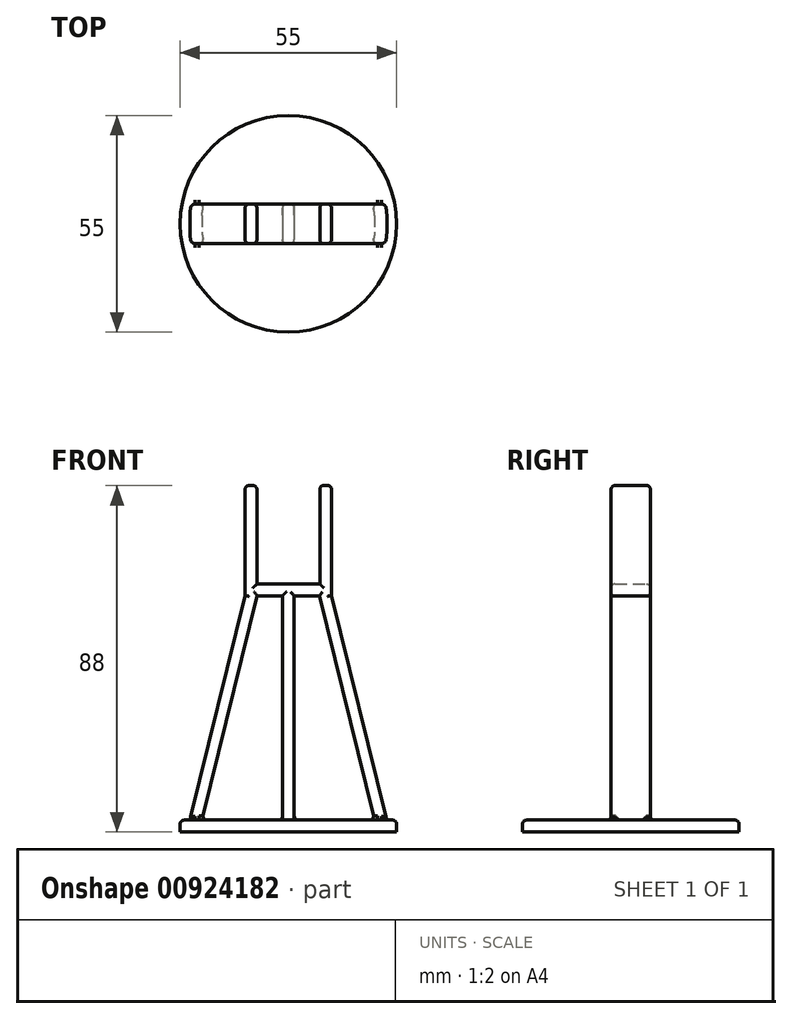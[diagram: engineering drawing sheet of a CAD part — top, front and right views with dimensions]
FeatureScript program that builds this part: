
annotation { "Feature Type Name" : "Feature", "Feature Type Description" : "" }
export const myFeature = defineFeature(function(context is Context, id is Id, definition is map)
    precondition{}
    {
        {
            var Q0;
            Q0=qCreatedBy(makeId("Front.planeOp"),FACE);
            var sketch = newSketch(context, id + "F0", { "sketchPlane" : qUnion([Q0])});
            skLineSegment(sketch, "E0.left", {"start": v(8, 12.5) * mm, "end": v(8, -12.5) * mm});
            skLineSegment(sketch, "E0.right", {"start": v(-8, 12.5) * mm, "end": v(-8, -12.5) * mm});
            skPoint(sketch, "E0.middle", {"position": v(0, 0) * mm});
            skLineSegment(sketch, "E1.top", {"start": v(-25, -72.5) * mm, "end": v(25, -72.5) * mm});
            skLineSegment(sketch, "E2", {"start": v(8, -12.5) * mm, "end": v(-8, -12.5) * mm});
            skLineSegment(sketch, "E3.0", {"start": v(11, 12.5) * mm, "end": v(11, -15.5) * mm});
            skLineSegment(sketch, "E3.1", {"start": v(11, -15.5) * mm, "end": v(-11, -15.5) * mm});
            skLineSegment(sketch, "E3.2", {"start": v(-11, 12.5) * mm, "end": v(-11, -15.5) * mm});
            skLineSegment(sketch, "E4", {"start": v(-8, 12.5) * mm, "end": v(-11, 12.5) * mm});
            skLineSegment(sketch, "E5", {"start": v(8, 12.5) * mm, "end": v(11, 12.5) * mm});
            skLineSegment(sketch, "E6", {"start": v(-11, -15.5) * mm, "end": v(-25, -72.5) * mm});
            skLineSegment(sketch, "E7", {"start": v(11, -15.5) * mm, "end": v(25, -72.5) * mm});
            skSolve(sketch);
        }
        {
            var Q0;
            Q0 = qSketchRegion(id + "F0", true);
            extrude(context, id + "F1", {"entities" : qUnion([Q0]), "depth" : 10 * mm, "offsetDistance" : 25 * mm});
        }
        {
            var Q0;
            Q0=makeQuery(id+"F1.opExtrude","CAP_FACE",FACE,{"disambiguationData":[OSD([sQuery(id+"F0.wireOp",EDGE,"E0.left"),sQuery(id+"F0.wireOp",EDGE,"E0.right"),sQuery(id+"F0.wireOp",EDGE,"E1.top"),sQuery(id+"F0.wireOp",EDGE,"E2"),sQuery(id+"F0.wireOp",EDGE,"E3.0"),sQuery(id+"F0.wireOp",EDGE,"E3.2"),sQuery(id+"F0.wireOp",EDGE,"E4"),sQuery(id+"F0.wireOp",EDGE,"E5"),sQuery(id+"F0.wireOp",EDGE,"E6"),sQuery(id+"F0.wireOp",EDGE,"E7")])],"isStart":false});
            var sketch = newSketch(context, id + "F2", { "sketchPlane" : qUnion([Q0])});
            skLineSegment(sketch, "E8", {"start": v(-11, -15.5) * mm, "end": v(11, -15.5) * mm, "construction": true});
            skLineSegment(sketch, "E9", {"start": v(-7.91, -15.5) * mm, "end": v(-21.91, -72.5) * mm});
            skLineSegment(sketch, "E10", {"start": v(-21.91, -72.5) * mm, "end": v(-1.5, -72.5) * mm});
            skLineSegment(sketch, "E11", {"start": v(-1.5, -72.5) * mm, "end": v(-1.5, -15.5) * mm});
            skLineSegment(sketch, "E12", {"start": v(-1.5, -15.5) * mm, "end": v(-7.91, -15.5) * mm});
            skLineSegment(sketch, "E13.MirrorCS", {"start": v(1.5, -72.5) * mm, "end": v(1.5, -15.5) * mm});
            skLineSegment(sketch, "E14.MirrorCS", {"start": v(7.91, -15.5) * mm, "end": v(21.91, -72.5) * mm});
            skLineSegment(sketch, "E15.MirrorCS", {"start": v(11, -15.5) * mm, "end": v(-11, -15.5) * mm, "construction": true});
            skLineSegment(sketch, "E16.MirrorCS", {"start": v(21.91, -72.5) * mm, "end": v(1.5, -72.5) * mm});
            skLineSegment(sketch, "E17", {"start": v(7.91, -15.5) * mm, "end": v(1.5, -15.5) * mm});
            skSolve(sketch);
        }
        {
            var Q0;
            Q0 = qSketchRegion(id + "F2", true);
            extrude(context, id + "F3", {"entities" : qUnion([Q0]), "operationType" : NewBodyOperationType.REMOVE, "oppositeDirection" : true, "depth" : 25 * mm, "offsetDistance" : 25 * mm});
        }
        {
            var Q0;
            Q0=makeQuery(id+"F1.opExtrude","SWEPT_FACE",FACE,{"disambiguationData":[OSD([sQuery(id+"F0.wireOp",EDGE,"E1.top")])]});
            var sketch = newSketch(context, id + "F4", { "sketchPlane" : qUnion([Q0])});
            skCircle(sketch, "E18", {"center": v(0, 5) * mm, "radius": 27.5 * mm});
            skLineSegment(sketch, "E19", {"start": v(0, 5) * mm, "end": v(0, 0) * mm, "construction": true});
            skLineSegment(sketch, "E20", {"start": v(0, 5) * mm, "end": v(0, 10) * mm, "construction": true});
            skLineSegment(sketch, "E21", {"start": v(0, 5) * mm, "end": v(-1.5, 5) * mm, "construction": true});
            skLineSegment(sketch, "E22", {"start": v(0, 5) * mm, "end": v(1.5, 5) * mm, "construction": true});
            skSolve(sketch);
        }
        {
            var Q0;
            Q0 = qSketchRegion(id + "F4", true);
            extrude(context, id + "F5", {"entities" : qUnion([Q0]), "operationType" : NewBodyOperationType.ADD, "depth" : 3 * mm, "offsetDistance" : 25 * mm});
        }
        {
            var Q0;
            Q0=makeQuery(id+"F1.opExtrude","SWEPT_EDGE",EDGE,{"disambiguationData":[OSD([sQuery(id+"F0.wireOp",EDGE,"E0.right"),sQuery(id+"F0.wireOp",EDGE,"E4")])]});
            var Q1;
            Q1=makeQuery(id+"F1.opExtrude","SWEPT_EDGE",EDGE,{"disambiguationData":[OSD([sQuery(id+"F0.wireOp",EDGE,"E0.left"),sQuery(id+"F0.wireOp",EDGE,"E5")])]});
            var Q2;
            Q2=makeQuery(id+"F1.opExtrude","SWEPT_EDGE",EDGE,{"disambiguationData":[OSD([sQuery(id+"F0.wireOp",EDGE,"E3.0"),sQuery(id+"F0.wireOp",EDGE,"E5")])]});
            var Q3;
            Q3=makeQuery(id+"F1.opExtrude","SWEPT_EDGE",EDGE,{"disambiguationData":[OSD([sQuery(id+"F0.wireOp",EDGE,"E3.2"),sQuery(id+"F0.wireOp",EDGE,"E4")])]});
            var Q4;
            Q4=makeQuery(id+"F1.opExtrude","CAP_EDGE",EDGE,{"disambiguationData":[OSD([sQuery(id+"F0.wireOp",EDGE,"E5")])],"isStart":false});
            var Q5;
            Q5=makeQuery(id+"F1.opExtrude","CAP_EDGE",EDGE,{"disambiguationData":[OSD([sQuery(id+"F0.wireOp",EDGE,"E4")])],"isStart":false});
            var Q6;
            Q6=makeQuery(id+"F1.opExtrude","CAP_EDGE",EDGE,{"disambiguationData":[OSD([sQuery(id+"F0.wireOp",EDGE,"E5")])],"isStart":true});
            var Q7;
            Q7=makeQuery(id+"F1.opExtrude","CAP_EDGE",EDGE,{"disambiguationData":[OSD([sQuery(id+"F0.wireOp",EDGE,"E4")])],"isStart":true});
            var Q8;
            Q8=makeQuery(id+"F1.opExtrude","CAP_EDGE",EDGE,{"disambiguationData":[OSD([sQuery(id+"F0.wireOp",EDGE,"E3.2")])],"isStart":true});
            var Q9;
            Q9=makeQuery(id+"F1.opExtrude","CAP_EDGE",EDGE,{"disambiguationData":[OSD([sQuery(id+"F0.wireOp",EDGE,"E3.0")])],"isStart":true});
            var Q10;
            Q10=makeQuery(id+"F1.opExtrude","CAP_EDGE",EDGE,{"disambiguationData":[OSD([sQuery(id+"F0.wireOp",EDGE,"E3.0")])],"isStart":false});
            var Q11;
            Q11=makeQuery(id+"F1.opExtrude","CAP_EDGE",EDGE,{"disambiguationData":[OSD([sQuery(id+"F0.wireOp",EDGE,"E3.2")])],"isStart":false});
            var Q12;
            Q12=makeQuery(id+"F1.opExtrude","CAP_EDGE",EDGE,{"disambiguationData":[OSD([sQuery(id+"F0.wireOp",EDGE,"E6")])],"isStart":false});
            var Q13;
            Q13=makeQuery(id+"F1.opExtrude","CAP_EDGE",EDGE,{"disambiguationData":[OSD([sQuery(id+"F0.wireOp",EDGE,"E7")])],"isStart":false});
            var Q14;
            Q14=makeQuery(id+"F1.opExtrude","CAP_EDGE",EDGE,{"disambiguationData":[OSD([sQuery(id+"F0.wireOp",EDGE,"E6")])],"isStart":true});
            var Q15;
            Q15=makeQuery(id+"F1.opExtrude","CAP_EDGE",EDGE,{"disambiguationData":[OSD([sQuery(id+"F0.wireOp",EDGE,"E7")])],"isStart":true});
            var Q16;
            Q16=makeQuery(id+"F5.opExtrude","CAP_EDGE",EDGE,{"disambiguationData":[OSD([sQuery(id+"F4.wireOp",EDGE,"BOZRl56y-XAUw-6Jbv-m02X-E17xRCYPpdMF")])],"isStart":true});
            var Q17;
            Q17=makeQuery(id+"F1.opExtrude","CAP_EDGE",EDGE,{"disambiguationData":[OSD([sQuery(id+"F0.wireOp",EDGE,"E1.top")])],"isStart":false});
            var Q18;
            Q18=makeQuery(id+"F1.opExtrude","CAP_FACE",FACE,{"disambiguationData":[OSD([sQuery(id+"F0.wireOp",EDGE,"E0.left"),sQuery(id+"F0.wireOp",EDGE,"E0.right"),sQuery(id+"F0.wireOp",EDGE,"E1.top"),sQuery(id+"F0.wireOp",EDGE,"E2"),sQuery(id+"F0.wireOp",EDGE,"E3.0"),sQuery(id+"F0.wireOp",EDGE,"E3.2"),sQuery(id+"F0.wireOp",EDGE,"E4"),sQuery(id+"F0.wireOp",EDGE,"E5"),sQuery(id+"F0.wireOp",EDGE,"E6"),sQuery(id+"F0.wireOp",EDGE,"E7")])],"isStart":false});
            var Q19;
            Q19=makeQuery(id+"F1.opExtrude","CAP_FACE",FACE,{"disambiguationData":[OSD([sQuery(id+"F0.wireOp",EDGE,"E0.left"),sQuery(id+"F0.wireOp",EDGE,"E0.right"),sQuery(id+"F0.wireOp",EDGE,"E1.top"),sQuery(id+"F0.wireOp",EDGE,"E2"),sQuery(id+"F0.wireOp",EDGE,"E3.0"),sQuery(id+"F0.wireOp",EDGE,"E3.2"),sQuery(id+"F0.wireOp",EDGE,"E4"),sQuery(id+"F0.wireOp",EDGE,"E5"),sQuery(id+"F0.wireOp",EDGE,"E6"),sQuery(id+"F0.wireOp",EDGE,"E7")])],"isStart":true});
            var Q20;
            Q20=makeQuery(id+"F5.opExtrude","CAP_EDGE",EDGE,{"disambiguationData":[OSD([sQuery(id+"F4.wireOp",EDGE,"E18")])],"isStart":true});
            fillet(context, id + "F6", {"entities" : qUnion([Q0, Q1, Q2, Q3, Q4, Q5, Q6, Q7, Q8, Q9, Q10, Q11, Q12, Q13, Q14, Q15, Q16, Q17, Q18, Q19, Q20]), "radius" : 1 * mm, "tangentPropagation" : true, "allowEdgeOverflow" : false});
        }
    });
